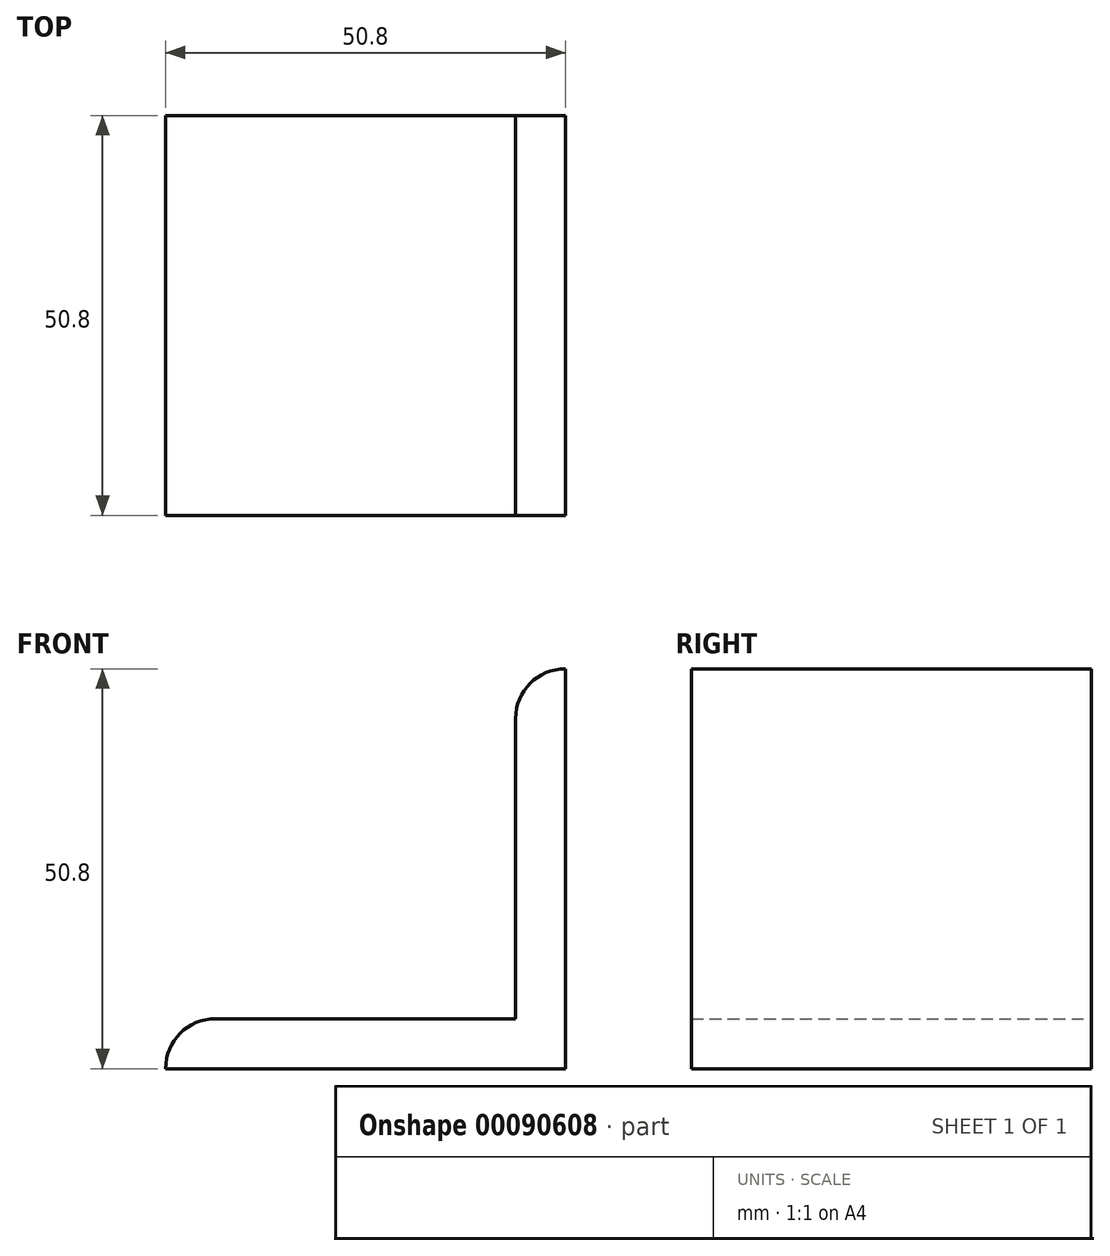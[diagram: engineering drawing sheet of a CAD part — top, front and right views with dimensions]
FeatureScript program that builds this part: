
annotation { "Feature Type Name" : "Feature", "Feature Type Description" : "" }
export const myFeature = defineFeature(function(context is Context, id is Id, definition is map)
    precondition{}
    {
        {
            var Q0;
            Q0=qCreatedBy(makeId("Front.planeOp"),FACE);
            var sketch = newSketch(context, id + "F0", { "sketchPlane" : qUnion([Q0])});
            skLineSegment(sketch, "E0", {"start": v(0, 0) * mm, "end": v(-50.8, 0) * mm});
            skLineSegment(sketch, "E1", {"start": v(-50.8, 0) * mm, "end": v(-50.8, 0) * mm});
            skLineSegment(sketch, "E2", {"start": v(-44.45, 6.35) * mm, "end": v(-6.35, 6.35) * mm});
            skLineSegment(sketch, "E3", {"start": v(-6.35, 6.35) * mm, "end": v(-6.35, 44.45) * mm});
            skLineSegment(sketch, "E4", {"start": v(0, 50.8) * mm, "end": v(0, 50.8) * mm});
            skLineSegment(sketch, "E5", {"start": v(0, 50.8) * mm, "end": v(0, 0) * mm});
            skPoint(sketch, "E6.visualSharp", {"position": v(-50.8, 6.35) * mm});
            skArc(sketch, "E6.filletArc", {"start": v(-44.45, 6.35) * mm, "mid": v(-48.94, 4.5) * mm, "end": v(-50.8, 0) * mm});
            skPoint(sketch, "E7.visualSharp", {"position": v(-6.35, 50.8) * mm});
            skArc(sketch, "E7.filletArc", {"start": v(0, 50.8) * mm, "mid": v(-4.5, 48.94) * mm, "end": v(-6.35, 44.45) * mm});
            skSolve(sketch);
        }
        {
            var Q0;
            Q0 = qSketchRegion(id + "F0", true);
            extrude(context, id + "F1", {"entities" : qUnion([Q0]), "endBound" : BoundingType.SYMMETRIC, "depth" : 50.8 * mm});
        }
    });
